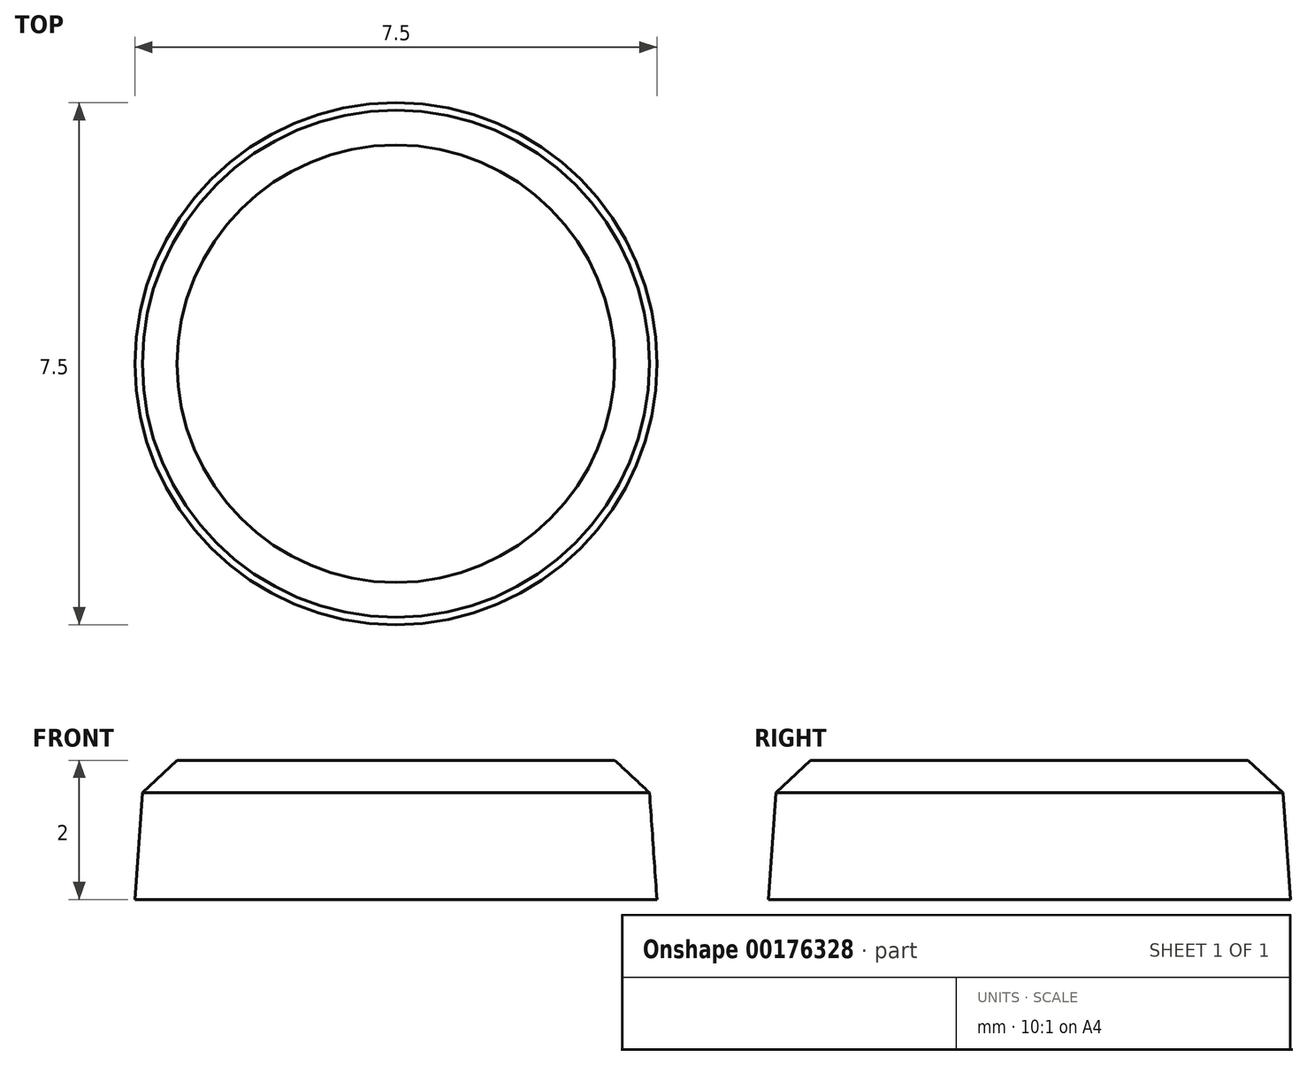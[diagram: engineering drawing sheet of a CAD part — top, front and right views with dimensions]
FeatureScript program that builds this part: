
annotation { "Feature Type Name" : "Feature", "Feature Type Description" : "" }
export const myFeature = defineFeature(function(context is Context, id is Id, definition is map)
    precondition{}
    {
        {
            var Q0;
            Q0=qCreatedBy(makeId("Top.planeOp"),FACE);
            var sketch = newSketch(context, id + "F0", { "sketchPlane" : qUnion([Q0])});
            skCircle(sketch, "E0", {"center": v(0, 0) * mm, "radius": 3.75 * mm});
            skSolve(sketch);
        }
        {
            var Q0;
            Q0 = qSketchRegion(id + "F0", true);
            extrude(context, id + "F1", {"entities" : qUnion([Q0]), "depth" : 2 * mm, "hasDraft" : true, "draftAngle" : 4 * degree, "draftPullDirection" : true});
        }
        {
            var Q0;
            Q0=makeQuery(id+"F1.opExtrude","CAP_EDGE",EDGE,{"disambiguationData":[OSD([sQuery(id+"F0.wireOp",EDGE,"E0")])],"isStart":false});
            chamfer(context, id + "F2", {"entities" : qUnion([Q0]), "width" : .5 * mm, "tangentPropagation" : true});
        }
    });
